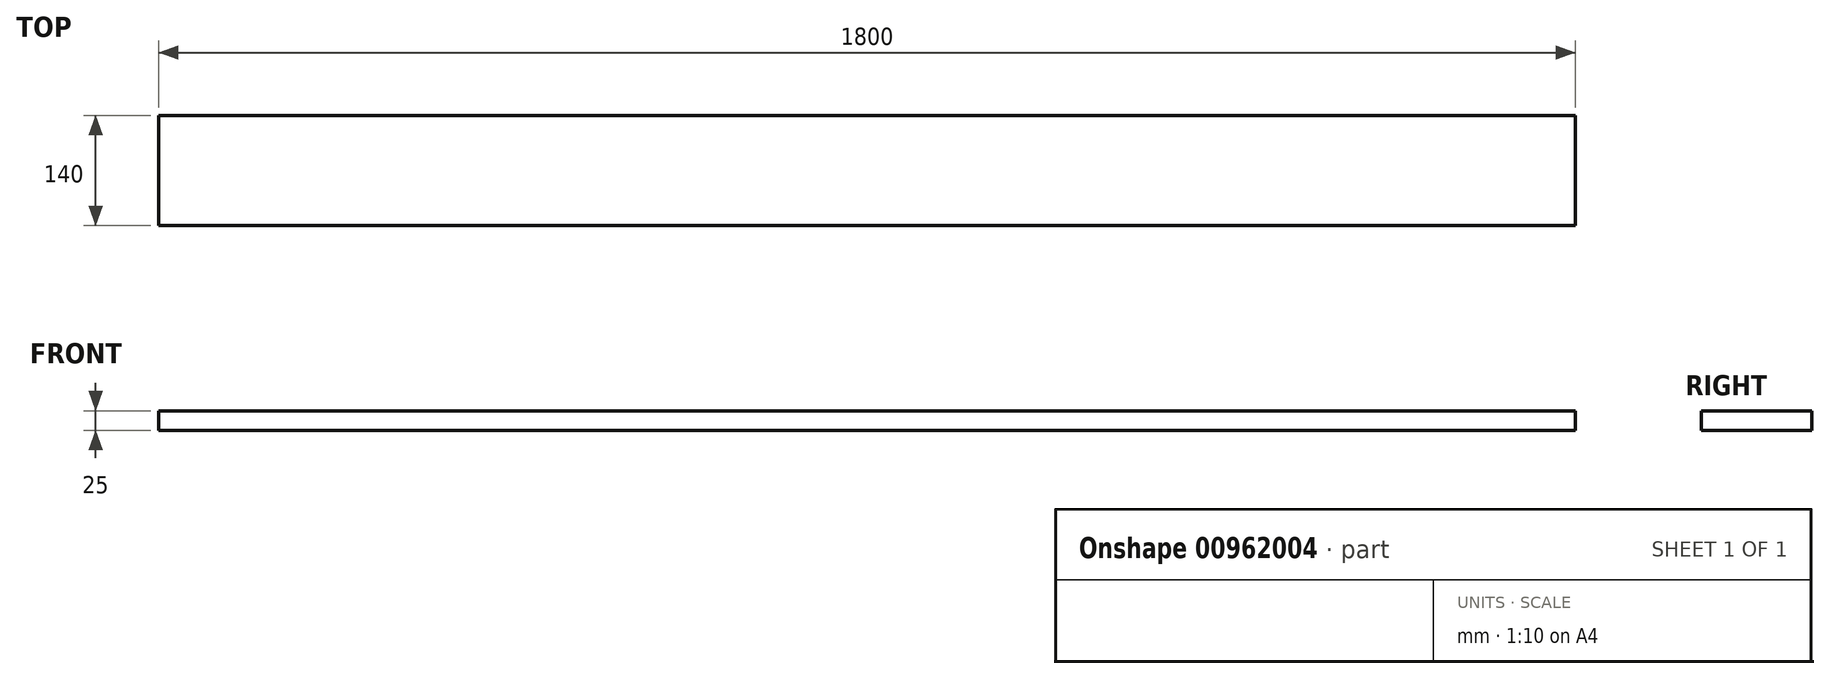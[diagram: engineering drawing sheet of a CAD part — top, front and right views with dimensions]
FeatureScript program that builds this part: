
annotation { "Feature Type Name" : "Feature", "Feature Type Description" : "" }
export const myFeature = defineFeature(function(context is Context, id is Id, definition is map)
    precondition{}
    {
        {
            var Q0;
            Q0=qCreatedBy(makeId("Top.planeOp"), FACE);
            var sketch = newSketch(context, id + "F0", { "sketchPlane" : qUnion([Q0])});
            skLineSegment(sketch, "E0.bottom", {"start": v(-997.9, -215.67) * mm, "end": v(802.1, -215.67) * mm});
            skLineSegment(sketch, "E0.top", {"start": v(-997.9, -75.67) * mm, "end": v(802.1, -75.67) * mm});
            skLineSegment(sketch, "E0.left", {"start": v(-997.9, -215.67) * mm, "end": v(-997.9, -75.67) * mm});
            skLineSegment(sketch, "E0.right", {"start": v(802.1, -215.67) * mm, "end": v(802.1, -75.67) * mm});
            skSolve(sketch);
        }
        {
            var Q0;
            Q0 = qSketchRegion(id + "F0", true);
            extrude(context, id + "F1", {"entities" : qUnion([Q0]), "domain" : OperationDomain.MODEL, "flatOperationType" : FlatOperationType.REMOVE, "depth" : 25 * mm, "offsetDistance" : 25 * mm});
        }
    });
